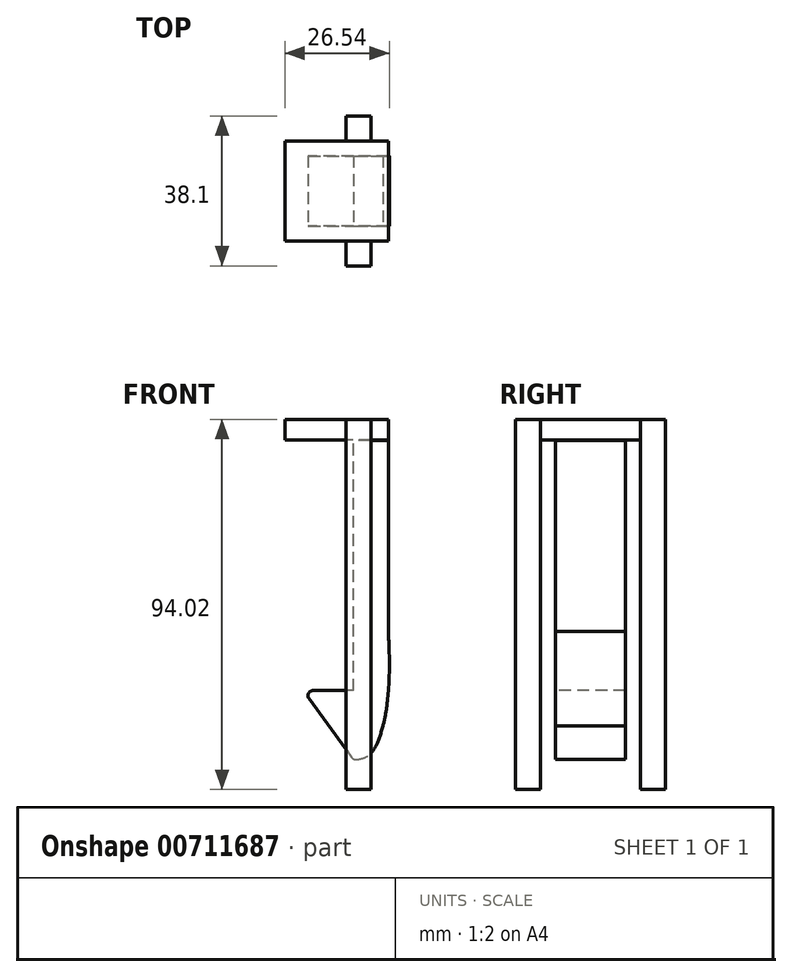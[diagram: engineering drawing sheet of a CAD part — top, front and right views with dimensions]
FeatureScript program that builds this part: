
annotation { "Feature Type Name" : "Feature", "Feature Type Description" : "" }
export const myFeature = defineFeature(function(context is Context, id is Id, definition is map)
    precondition{}
    {
        {
            var Q0;
            Q0=qCreatedBy(makeId("Front.planeOp"),FACE);
            var sketch = newSketch(context, id + "F0", { "sketchPlane" : qUnion([Q0])});
            skLineSegment(sketch, "E0.bottom", {"start": v(4.44, -31.75) * mm, "end": v(-4.45, -31.75) * mm});
            skLineSegment(sketch, "E0.top", {"start": v(4.45, 31.75) * mm, "end": v(-4.45, 31.75) * mm});
            skLineSegment(sketch, "E0.left", {"start": v(4.44, -31.75) * mm, "end": v(4.45, 31.75) * mm});
            skLineSegment(sketch, "E0.right", {"start": v(-4.45, -31.75) * mm, "end": v(-4.44, 31.75) * mm});
            skPoint(sketch, "E0.middle", {"position": v(0, 0) * mm});
            skLineSegment(sketch, "E1", {"start": v(-4.45, -31.75) * mm, "end": v(-17.24, -31.75) * mm});
            skLineSegment(sketch, "E2", {"start": v(-17.24, -31.75) * mm, "end": v(-4.45, -49.31) * mm});
            skFitSpline(sketch, "E3", {"points": [v(-4.44, -49.31) * mm, v(0, -47.66) * mm, v(4.45, -31.75) * mm, v(4.45, -16.68) * mm, v(4.45, -12.44) * mm], "startDerivative": vector(26.36, 2.28) * mm, "endDerivative": vector(0.48, 21.52) * mm});
            skFitSpline(sketch, "E4", {"points": [v(0, -47.66) * mm, v(3.04, -40.74) * mm, v(4.27, -33.62) * mm], "startDerivative": vector(6.85, 13.5) * mm, "endDerivative": vector(1.64, 14.58) * mm});
            skSolve(sketch);
        }
        {
            var Q0;
            Q0 = qSketchRegion(id + "F0", true);
            extrude(context, id + "F1", {"entities" : qUnion([Q0]), "endBound" : BoundingType.SYMMETRIC, "oppositeDirection" : true, "depth" : 17.78 * mm, "offsetDistance" : 25.4 * mm});
        }
        {
            var Q0;
            Q0=makeQuery(id+"F1.opExtrude","SWEPT_EDGE",EDGE,{"disambiguationData":[OSD([sQuery(id+"F0.wireOp",EDGE,"E1"),sQuery(id+"F0.wireOp",EDGE,"E2")])]});
            fillet(context, id + "F2", {"entities" : qUnion([Q0]), "radius" : 1.27 * mm, "tangentPropagation" : true, "allowEdgeOverflow" : false});
        }
        {
            var Q0;
            Q0=makeQuery(id+"F1.opExtrude","SWEPT_EDGE",EDGE,{"disambiguationData":[OSD([sQuery(id+"F0.wireOp",EDGE,"E2"),sQuery(id+"F0.wireOp",EDGE,"E3")])]});
            fillet(context, id + "F3", {"entities" : qUnion([Q0]), "radius" : 1.27 * mm, "tangentPropagation" : true, "allowEdgeOverflow" : false});
        }
        {
            var Q0;
            Q0=qCreatedBy(makeId("Front.planeOp"),FACE);
            var sketch = newSketch(context, id + "F4", { "sketchPlane" : qUnion([Q0])});
            skLineSegment(sketch, "E5.bottom", {"start": v(4.52, 31.99) * mm, "end": v(-21.85, 31.99) * mm});
            skLineSegment(sketch, "E5.top", {"start": v(4.52, 37.15) * mm, "end": v(-21.85, 37.15) * mm});
            skLineSegment(sketch, "E5.left", {"start": v(4.52, 31.99) * mm, "end": v(4.52, 37.15) * mm});
            skLineSegment(sketch, "E5.right", {"start": v(-21.85, 31.99) * mm, "end": v(-21.85, 37.15) * mm});
            skSolve(sketch);
        }
        {
            var Q0;
            Q0 = qSketchRegion(id + "F4", true);
            extrude(context, id + "F5", {"entities" : qUnion([Q0]), "endBound" : BoundingType.SYMMETRIC, "depth" : 25.4 * mm, "offsetDistance" : 25.4 * mm});
        }
        {
            var Q0;
            Q0=qCreatedBy(makeId("Right.planeOp"),FACE);
            var sketch = newSketch(context, id + "F6", { "sketchPlane" : qUnion([Q0])});
            skLineSegment(sketch, "E6.bottom", {"start": v(12.7, 37.15) * mm, "end": v(19.05, 37.15) * mm});
            skLineSegment(sketch, "E6.top", {"start": v(12.7, -56.87) * mm, "end": v(19.05, -56.87) * mm});
            skLineSegment(sketch, "E6.left", {"start": v(12.7, 37.15) * mm, "end": v(12.7, -56.87) * mm});
            skLineSegment(sketch, "E6.right", {"start": v(19.05, 37.15) * mm, "end": v(19.05, -56.87) * mm});
            skLineSegment(sketch, "E7.bottom", {"start": v(-12.7, 37.15) * mm, "end": v(-19.05, 37.15) * mm});
            skLineSegment(sketch, "E7.top", {"start": v(-12.7, -56.87) * mm, "end": v(-19.05, -56.87) * mm});
            skLineSegment(sketch, "E7.left", {"start": v(-12.7, 37.15) * mm, "end": v(-12.7, -56.87) * mm});
            skLineSegment(sketch, "E7.right", {"start": v(-19.05, 37.15) * mm, "end": v(-19.05, -56.87) * mm});
            skLineSegment(sketch, "E8.left", {"start": v(12.7, -56.87) * mm, "end": v(12.7, -51.9) * mm});
            skLineSegment(sketch, "E8.right", {"start": v(-12.7, -56.69) * mm, "end": v(-12.7, -51.71) * mm});
            skLineSegment(sketch, "E9", {"start": v(12.7, -51.9) * mm, "end": v(-12.7, -51.71) * mm});
            skLineSegment(sketch, "E10", {"start": v(12.7, -56.87) * mm, "end": v(-12.7, -56.69) * mm});
            skSolve(sketch);
        }
        {
            var Q0;
            Q0=makeQuery(id+"F6.imprint","IMPRINT",FACE,{"disambiguationData":[TD([[makeQuery(id+"F6.imprint","IMPRINT",EDGE,{"derivedFrom":sQuery(id+"F6.wireOp",EDGE,"E6.bottom")}),-1.0]])]});
            var Q1;
            Q1=makeQuery(id+"F6.imprint","IMPRINT",FACE,{"disambiguationData":[TD([[makeQuery(id+"F6.imprint","IMPRINT",EDGE,{"derivedFrom":sQuery(id+"F6.wireOp",EDGE,"E8.left")}),1.0]])]});
            var Q2;
            {var subQ3=sQuery(id+"F6.wireOp",EDGE,"E7.bottom");Q2=makeQuery(id+"F6.imprint","IMPRINT",FACE,{"disambiguationData":[TD([[makeQuery(id+"F6.imprint","IMPRINT",EDGE,{"derivedFrom":subQ3}),1.0]])]});}
            extrude(context, id + "F7", {"entities" : qUnion([Q0, Q1, Q2]), "oppositeDirection" : true, "depth" : 6.35 * mm, "offsetDistance" : 25.4 * mm});
        }
    });
